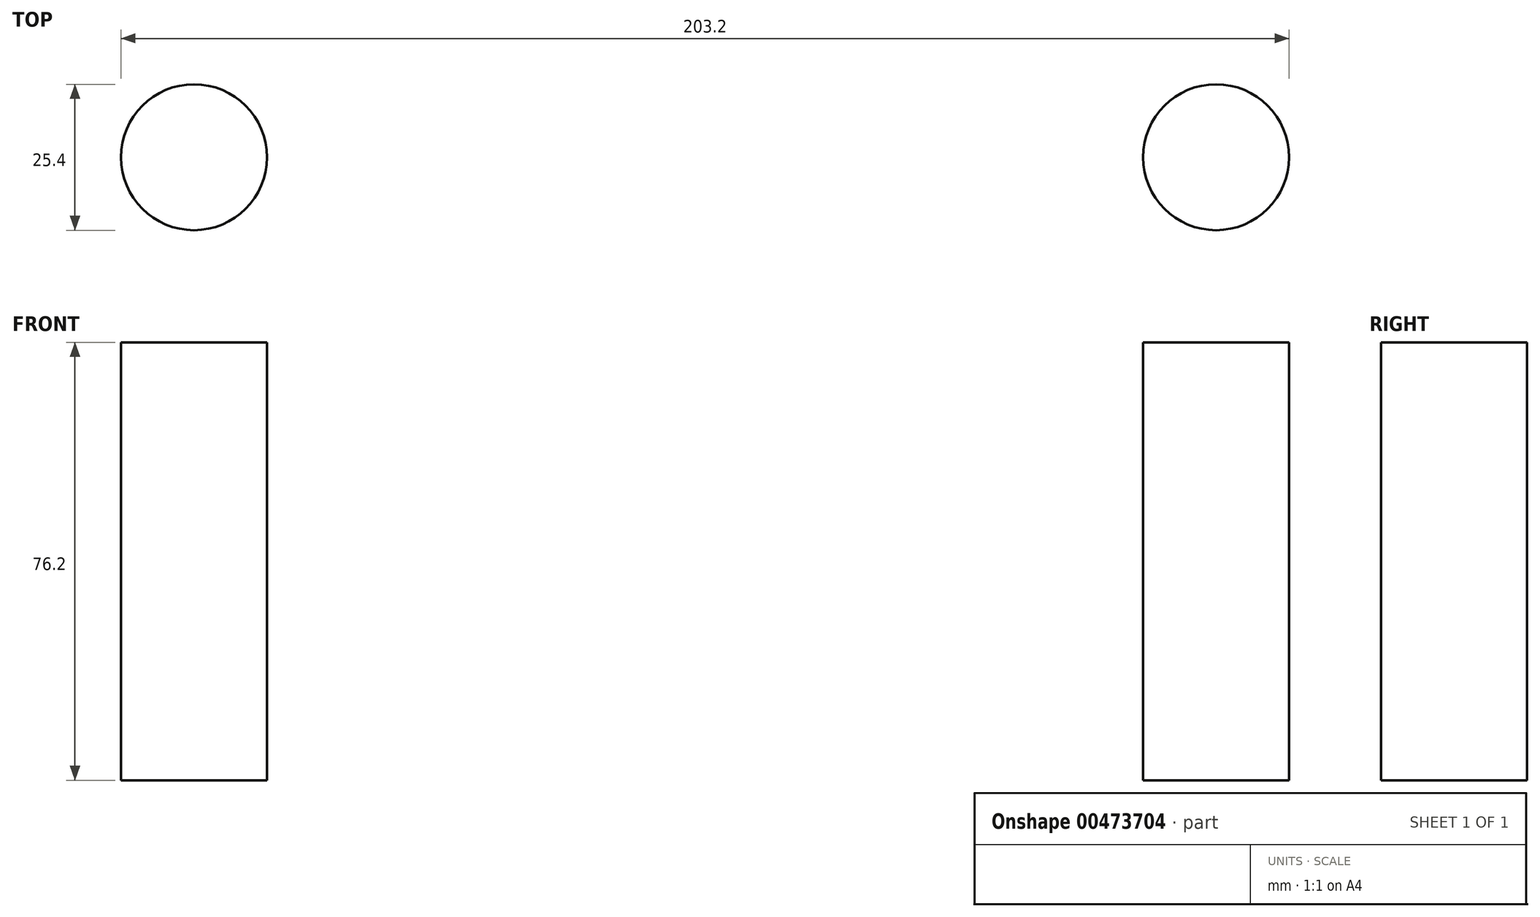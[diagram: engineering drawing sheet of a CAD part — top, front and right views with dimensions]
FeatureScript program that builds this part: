
annotation { "Feature Type Name" : "Feature", "Feature Type Description" : "" }
export const myFeature = defineFeature(function(context is Context, id is Id, definition is map)
    precondition{}
    {
        {
            var Q0;
            Q0=qCreatedBy(makeId("Top.planeOp"),FACE);
            var sketch = newSketch(context, id + "F0", { "sketchPlane" : qUnion([Q0])});
            skLineSegment(sketch, "E0", {"start": v(0, 0) * mm, "end": v(177.8, 0) * mm});
            skCircle(sketch, "E1", {"center": v(177.8, 0) * mm, "radius": 12.7 * mm});
            skCircle(sketch, "E2", {"center": v(0, 0) * mm, "radius": 12.7 * mm});
            skSolve(sketch);
        }
        {
            var Q0;
            Q0=makeQuery(id+"F0.imprint","IMPRINT",FACE,{"disambiguationData":[TD([[makeQuery(id+"F0.imprint","IMPRINT",EDGE,{"derivedFrom":sQuery(id+"F0.wireOp",EDGE,"E1")}),1.0]])]});
            var Q1;
            Q1=makeQuery(id+"F0.imprint","IMPRINT",FACE,{"disambiguationData":[TD([[makeQuery(id+"F0.imprint","IMPRINT",EDGE,{"derivedFrom":sQuery(id+"F0.wireOp",EDGE,"E2")}),1.0]])]});
            extrude(context, id + "F1", {"entities" : qUnion([Q0, Q1]), "depth" : 76.2 * mm});
        }
    });
